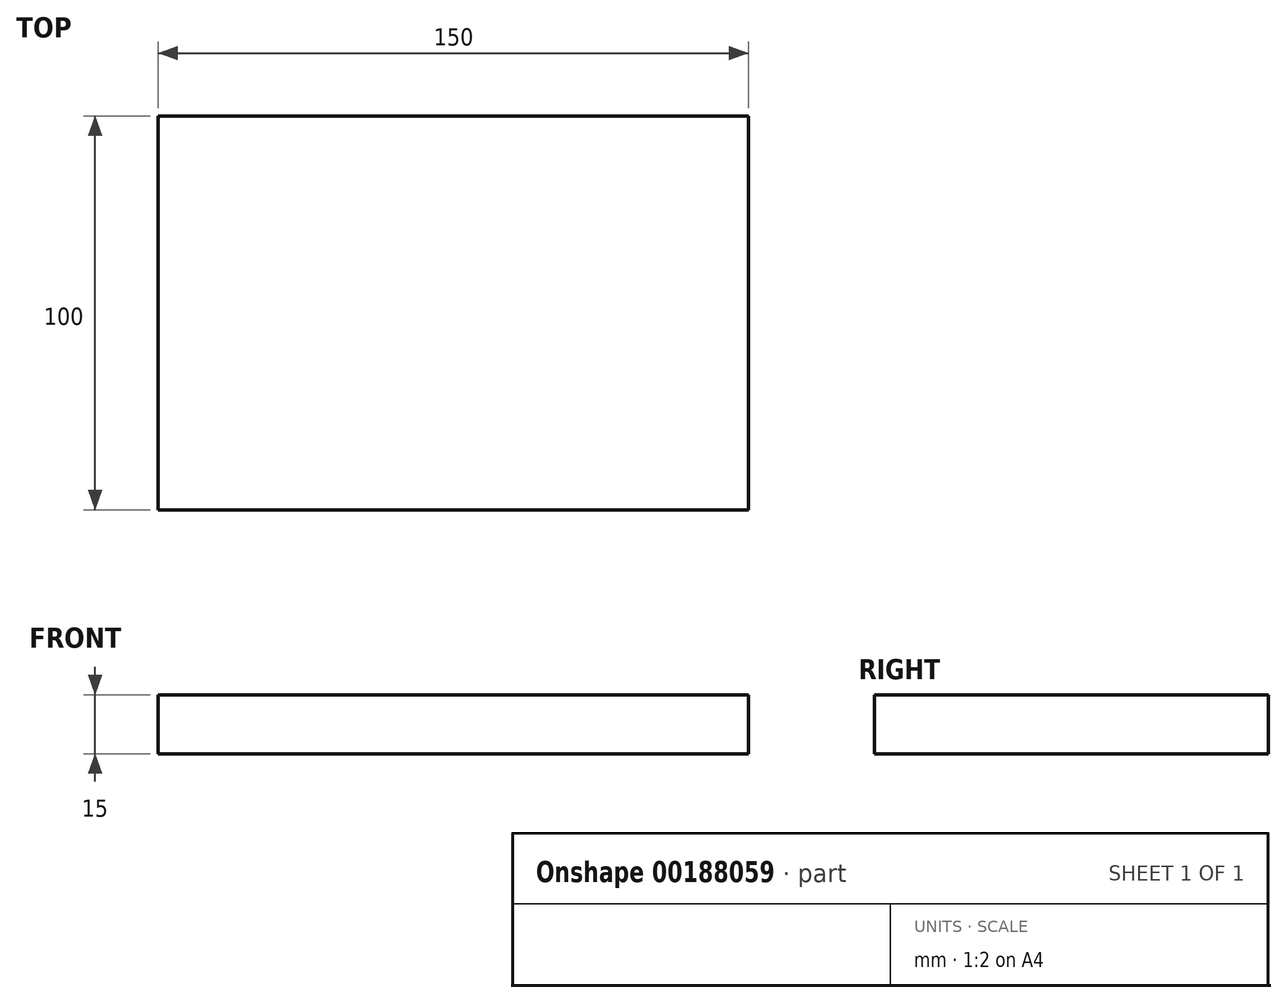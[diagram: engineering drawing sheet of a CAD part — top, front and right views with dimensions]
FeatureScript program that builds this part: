
annotation { "Feature Type Name" : "Feature", "Feature Type Description" : "" }
export const myFeature = defineFeature(function(context is Context, id is Id, definition is map)
    precondition{}
    {
        {
            var Q0;
            Q0=qCreatedBy(makeId("Top.planeOp"),FACE);
            var sketch = newSketch(context, id + "F0", { "sketchPlane" : qUnion([Q0])});
            skLineSegment(sketch, "E0.bottom", {"start": v(75, -50) * mm, "end": v(-75, -50) * mm});
            skLineSegment(sketch, "E0.top", {"start": v(75, 50) * mm, "end": v(-75, 50) * mm});
            skLineSegment(sketch, "E0.left", {"start": v(75, -50) * mm, "end": v(75, 50) * mm});
            skLineSegment(sketch, "E0.right", {"start": v(-75, -50) * mm, "end": v(-75, 50) * mm});
            skPoint(sketch, "E0.middle", {"position": v(0, 0) * mm});
            skSolve(sketch);
        }
        {
            var Q0;
            Q0=makeQuery(id+"F0.imprint","IMPRINT",FACE,{"disambiguationData":[TD([[makeQuery(id+"F0.imprint","IMPRINT",EDGE,{"derivedFrom":sQuery(id+"F0.wireOp",EDGE,"E0.bottom")}),-1.0]])]});
            extrude(context, id + "F1", {"entities" : qUnion([Q0]), "depth" : 15 * mm});
        }
        {
            var Q0;
            Q0=qCreatedBy(makeId("Top.planeOp"),FACE);
            var sketch = newSketch(context, id + "F2", { "sketchPlane" : qUnion([Q0])});
            skCircle(sketch, "E1", {"center": v(0, 0) * mm, "radius": 20.64 * mm});
            skSolve(sketch);
        }
        {
            var Q0;
            Q0=sQuery(id+"F2.wireOp",EDGE,"E1");
            extrude(context, id + "F3", {"bodyType" : ToolBodyType.SURFACE, "surfaceEntities" : qUnion([Q0]), "depth" : 30 * mm});
        }
    });
